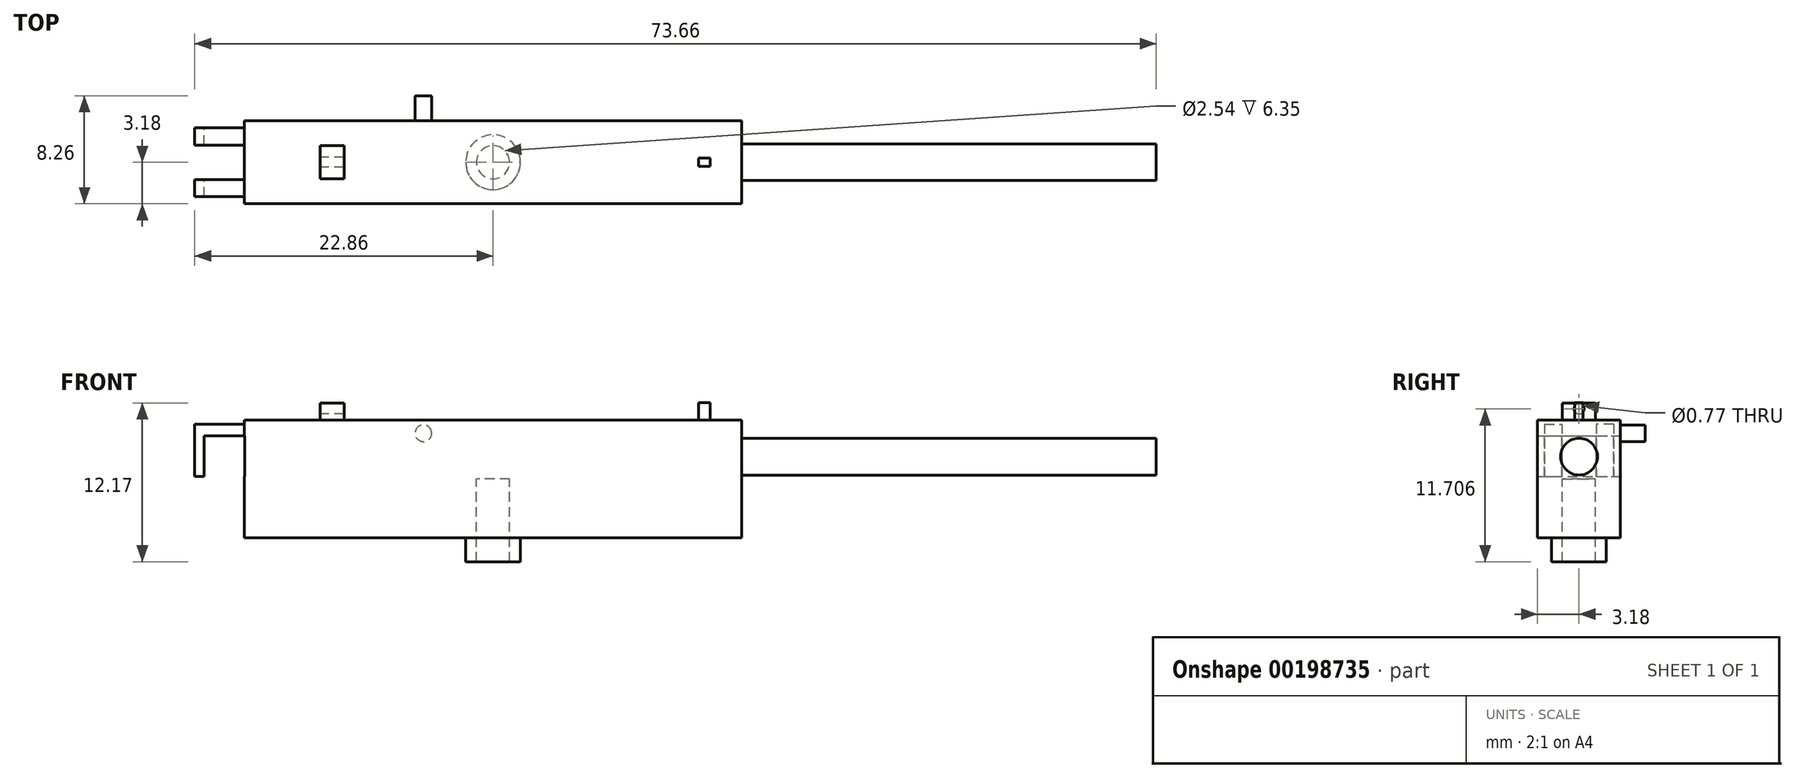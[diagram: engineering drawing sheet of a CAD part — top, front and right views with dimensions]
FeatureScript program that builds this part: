
annotation { "Feature Type Name" : "Feature", "Feature Type Description" : "" }
export const myFeature = defineFeature(function(context is Context, id is Id, definition is map)
    precondition{}
    {
        {
            var Q0;
            Q0=qCreatedBy(makeId("Front.planeOp"),FACE);
            var sketch = newSketch(context, id + "F0", { "sketchPlane" : qUnion([Q0])});
            skLineSegment(sketch, "E0.bottom", {"start": v(19.05, 4.5) * mm, "end": v(-19.05, 4.5) * mm});
            skLineSegment(sketch, "E0.top", {"start": v(19.05, -4.5) * mm, "end": v(-19.05, -4.5) * mm});
            skLineSegment(sketch, "E0.left", {"start": v(19.05, 4.5) * mm, "end": v(19.05, -4.5) * mm});
            skLineSegment(sketch, "E0.right", {"start": v(-19.05, 4.5) * mm, "end": v(-19.05, -4.5) * mm});
            skPoint(sketch, "E0.middle", {"position": v(0, 0) * mm});
            skSolve(sketch);
        }
        {
            var Q0;
            Q0 = qSketchRegion(id + "F0", true);
            extrude(context, id + "F1", {"entities" : qUnion([Q0]), "endBound" : BoundingType.SYMMETRIC, "depth" : 6.35 * mm});
        }
        {
            var Q0;
            Q0=qCreatedBy(makeId("Right.planeOp"),FACE);
            var sketch = newSketch(context, id + "F2", { "sketchPlane" : qUnion([Q0])});
            skLineSegment(sketch, "E1.bottom", {"start": v(2.64, 4.2) * mm, "end": v(1.32, 4.2) * mm});
            skLineSegment(sketch, "E1.top", {"start": v(2.64, 0.18) * mm, "end": v(1.32, 0.18) * mm});
            skLineSegment(sketch, "E1.left", {"start": v(2.64, 4.2) * mm, "end": v(2.64, 0.18) * mm});
            skLineSegment(sketch, "E1.right", {"start": v(1.32, 4.2) * mm, "end": v(1.32, 0.18) * mm});
            skLineSegment(sketch, "E2.MirrorCS", {"start": v(-1.32, 4.2) * mm, "end": v(-1.32, 0.18) * mm});
            skLineSegment(sketch, "E3.MirrorCS", {"start": v(-2.64, 4.2) * mm, "end": v(-1.32, 4.2) * mm});
            skLineSegment(sketch, "E4.MirrorCS", {"start": v(-2.64, 4.2) * mm, "end": v(-2.64, 0.18) * mm});
            skLineSegment(sketch, "E5.MirrorCS", {"start": v(-2.64, 0.18) * mm, "end": v(-1.32, 0.18) * mm});
            skSolve(sketch);
        }
        {
            var Q0;
            Q0 = qSketchRegion(id + "F2", true);
            extrude(context, id + "F3", {"entities" : qUnion([Q0]), "operationType" : NewBodyOperationType.ADD, "oppositeDirection" : true, "depth" : 22.86 * mm});
        }
        {
            var Q0;
            Q0=qCreatedBy(makeId("Front.planeOp"),FACE);
            var sketch = newSketch(context, id + "F4", { "sketchPlane" : qUnion([Q0])});
            skLineSegment(sketch, "E6.bottom", {"start": v(-19.04, 3.29) * mm, "end": v(-22.13, 3.29) * mm});
            skLineSegment(sketch, "E6.top", {"start": v(-19.04, 0.18) * mm, "end": v(-22.13, 0.18) * mm});
            skLineSegment(sketch, "E6.left", {"start": v(-19.04, 3.29) * mm, "end": v(-19.04, 0.18) * mm});
            skLineSegment(sketch, "E6.right", {"start": v(-22.13, 3.29) * mm, "end": v(-22.13, 0.18) * mm});
            skSolve(sketch);
        }
        {
            var Q0;
            Q0 = qSketchRegion(id + "F4", true);
            extrude(context, id + "F5", {"entities" : qUnion([Q0]), "operationType" : NewBodyOperationType.REMOVE, "endBound" : BoundingType.SYMMETRIC, "depth" : 25.4 * mm});
        }
        {
            var Q0;
            Q0=qCreatedBy(makeId("Front.planeOp"),FACE);
            var sketch = newSketch(context, id + "F6", { "sketchPlane" : qUnion([Q0])});
            skCircle(sketch, "E7", {"center": v(-5.34, 3.5) * mm, "radius": 0.64 * mm});
            skSolve(sketch);
        }
        {
            var Q0;
            Q0 = qSketchRegion(id + "F6", true);
            extrude(context, id + "F7", {"entities" : qUnion([Q0]), "operationType" : NewBodyOperationType.ADD, "oppositeDirection" : true, "depth" : 5.08 * mm});
        }
        {
            var Q0;
            Q0=qCreatedBy(makeId("Right.planeOp"),FACE);
            var sketch = newSketch(context, id + "F8", { "sketchPlane" : qUnion([Q0])});
            skCircle(sketch, "E8", {"center": v(0, 1.7) * mm, "radius": 1.4 * mm});
            skSolve(sketch);
        }
        {
            var Q0;
            Q0 = qSketchRegion(id + "F8", true);
            extrude(context, id + "F9", {"entities" : qUnion([Q0]), "operationType" : NewBodyOperationType.ADD, "depth" : 50.8 * mm});
        }
        {
            var Q0;
            Q0=qCreatedBy(makeId("Top.planeOp"),FACE);
            var sketch = newSketch(context, id + "F10", { "sketchPlane" : qUnion([Q0])});
            skCircle(sketch, "E9", {"center": v(0, 0) * mm, "radius": 2.1 * mm});
            skSolve(sketch);
        }
        {
            var Q0;
            Q0 = qSketchRegion(id + "F10", true);
            extrude(context, id + "F11", {"entities" : qUnion([Q0]), "operationType" : NewBodyOperationType.ADD, "oppositeDirection" : true, "depth" : 6.35 * mm});
        }
        {
            var Q0;
            Q0=qCreatedBy(makeId("Top.planeOp"),FACE);
            var sketch = newSketch(context, id + "F12", { "sketchPlane" : qUnion([Q0])});
            skCircle(sketch, "E10", {"center": v(0, 0) * mm, "radius": 1.27 * mm});
            skSolve(sketch);
        }
        {
            var Q0;
            Q0 = qSketchRegion(id + "F12", true);
            extrude(context, id + "F13", {"entities" : qUnion([Q0]), "operationType" : NewBodyOperationType.REMOVE, "oppositeDirection" : true, "depth" : 25.4 * mm});
        }
        {
            var Q0;
            Q0=qCreatedBy(makeId("Front.planeOp"),FACE);
            var sketch = newSketch(context, id + "F14", { "sketchPlane" : qUnion([Q0])});
            skLineSegment(sketch, "E11.bottom", {"start": v(16.63, 4.51) * mm, "end": v(15.73, 4.51) * mm});
            skLineSegment(sketch, "E11.top", {"start": v(16.63, 5.82) * mm, "end": v(15.73, 5.82) * mm});
            skLineSegment(sketch, "E11.left", {"start": v(16.63, 4.51) * mm, "end": v(16.63, 5.82) * mm});
            skLineSegment(sketch, "E11.right", {"start": v(15.73, 4.51) * mm, "end": v(15.73, 5.82) * mm});
            skSolve(sketch);
        }
        {
            var Q0;
            Q0 = qSketchRegion(id + "F14", true);
            extrude(context, id + "F15", {"entities" : qUnion([Q0]), "endBound" : BoundingType.SYMMETRIC, "depth" : 0.64 * mm});
        }
        {
            var Q0;
            Q0=qCreatedBy(makeId("Front.planeOp"),FACE);
            var sketch = newSketch(context, id + "F16", { "sketchPlane" : qUnion([Q0])});
            skLineSegment(sketch, "E12.bottom", {"start": v(-11.42, 4.5) * mm, "end": v(-13.26, 4.5) * mm});
            skLineSegment(sketch, "E12.top", {"start": v(-11.42, 5.82) * mm, "end": v(-13.26, 5.82) * mm});
            skLineSegment(sketch, "E12.left", {"start": v(-11.42, 4.5) * mm, "end": v(-11.42, 5.82) * mm});
            skLineSegment(sketch, "E12.right", {"start": v(-13.26, 4.5) * mm, "end": v(-13.26, 5.82) * mm});
            skSolve(sketch);
        }
        {
            var Q0;
            Q0 = qSketchRegion(id + "F16", true);
            extrude(context, id + "F17", {"entities" : qUnion([Q0]), "endBound" : BoundingType.SYMMETRIC, "depth" : 2.54 * mm});
        }
        {
            var Q0;
            Q0=makeQuery(id+"F17.opExtrude","SWEPT_FACE",FACE,{"disambiguationData":[OSD([sQuery(id+"F16.wireOp",EDGE,"E12.right")])]});
            var sketch = newSketch(context, id + "F18", { "sketchPlane" : qUnion([Q0])});
            skCircle(sketch, "E13", {"center": v(0, 5.36) * mm, "radius": 0.39 * mm});
            skSolve(sketch);
        }
        {
            var Q0;
            Q0 = qSketchRegion(id + "F18", true);
            extrude(context, id + "F19", {"entities" : qUnion([Q0]), "operationType" : NewBodyOperationType.REMOVE, "oppositeDirection" : true, "depth" : 12.7 * mm});
        }
    });
